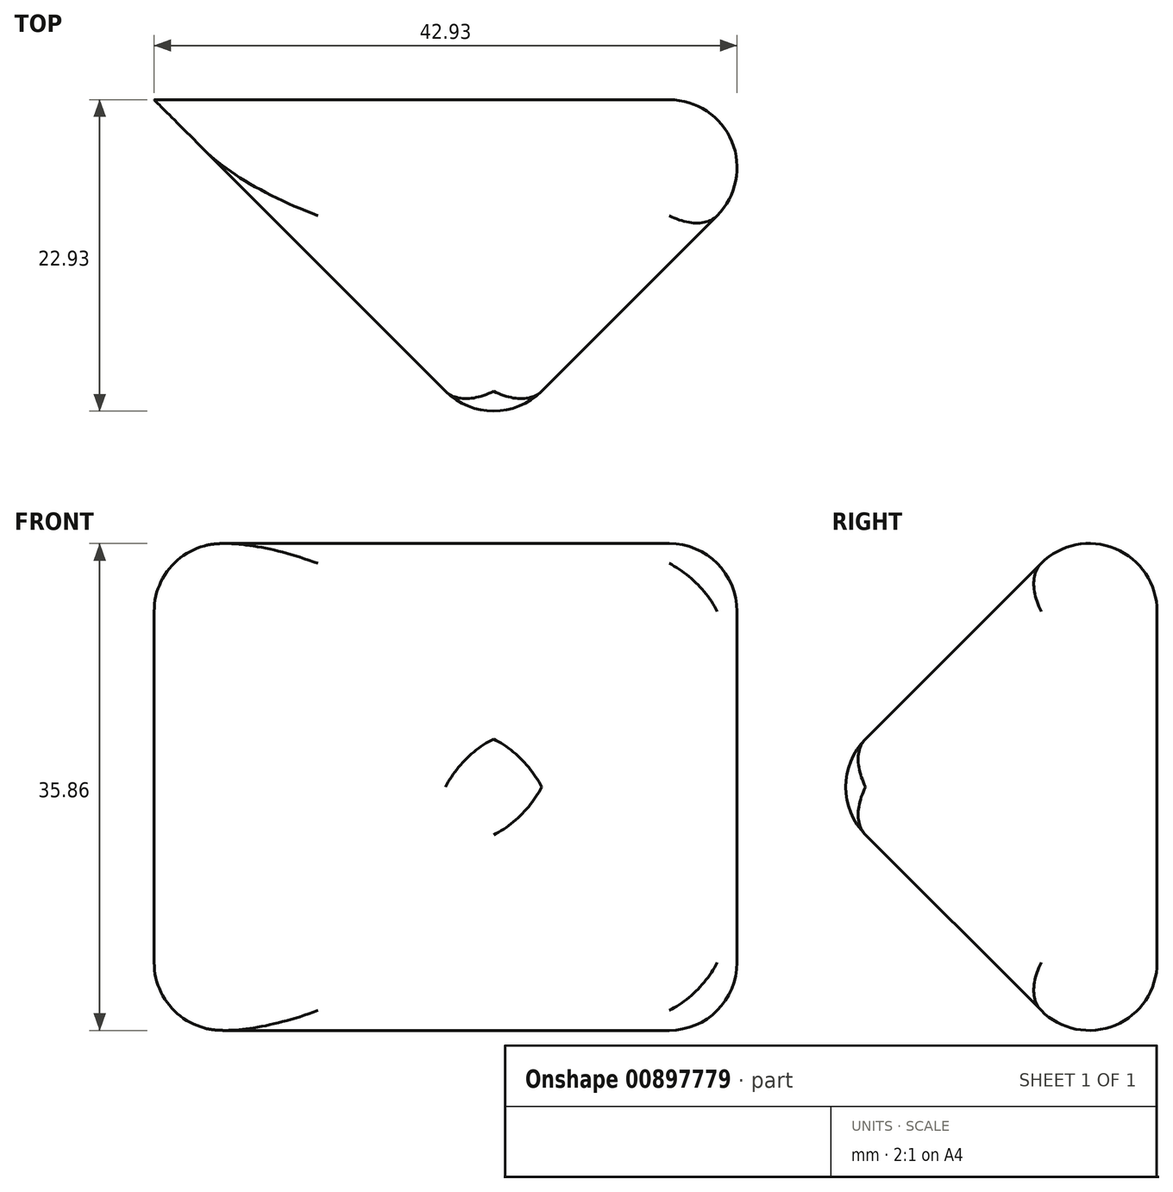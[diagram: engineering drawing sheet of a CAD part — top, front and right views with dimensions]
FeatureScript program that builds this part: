
annotation { "Feature Type Name" : "Feature", "Feature Type Description" : "" }
export const myFeature = defineFeature(function(context is Context, id is Id, definition is map)
    precondition{}
    {
        {
            var Q0;
            Q0=qCreatedBy(makeId("Front.planeOp"),FACE);
            var sketch = newSketch(context, id + "F0", { "sketchPlane" : qUnion([Q0])});
            skLineSegment(sketch, "E0.bottom", {"start": v(-50, 50) * mm, "end": v(0, 50) * mm});
            skLineSegment(sketch, "E0.top", {"start": v(-50, 0) * mm, "end": v(0, 0) * mm});
            skLineSegment(sketch, "E0.left", {"start": v(-50, 50) * mm, "end": v(-50, 0) * mm});
            skLineSegment(sketch, "E0.right", {"start": v(0, 50) * mm, "end": v(0, 0) * mm});
            skSolve(sketch);
        }
        {
            var Q0;
            Q0 = qSketchRegion(id + "F0", true);
            extrude(context, id + "F1", {"entities" : qUnion([Q0]), "depth" : 25 * mm, "offsetDistance" : 25 * mm, "hasDraft" : true, "draftAngle" : 45 * degree, "draftPullDirection" : true});
        }
        {
            var Q0;
            Q0=makeQuery(id+"F1.opExtrude","SWEPT_FACE",FACE,{"disambiguationData":[OSD([sQuery(id+"F0.wireOp",EDGE,"E0.top")])]});
            var Q1;
            Q1=makeQuery(id+"F1.opExtrude","SWEPT_FACE",FACE,{"disambiguationData":[OSD([sQuery(id+"F0.wireOp",EDGE,"E0.right")])]});
            var Q2;
            Q2=makeQuery(id+"F1.opExtrude","SWEPT_FACE",FACE,{"disambiguationData":[OSD([sQuery(id+"F0.wireOp",EDGE,"E0.bottom")])]});
            var Q3;
            Q3=makeQuery(id+"F1.opExtrude","SWEPT_EDGE",EDGE,{"disambiguationData":[OSD([sQuery(id+"F0.wireOp",EDGE,"E0.bottom"),sQuery(id+"F0.wireOp",EDGE,"E0.left")])]});
            var Q4;
            {var subQ0=sQuery(id+"F0.wireOp",EDGE,"E0.left");Q4=makeQuery(id+"F1.*.draft.opDraft","MERGE",FACE,{"derivedFrom":[makeQuery(id+"F1.opExtrude","CAP_FACE",FACE,{"disambiguationData":[OSD([sQuery(id+"F0.wireOp",EDGE,"E0.bottom"),sQuery(id+"F0.wireOp",EDGE,"E0.top"),subQ0,sQuery(id+"F0.wireOp",EDGE,"E0.right")])],"isStart":false}),makeQuery(id+"F1.opExtrude","SWEPT_FACE",FACE,{"disambiguationData":[OSD([subQ0])]})]});}
            fillet(context, id + "F2", {"entities" : qUnion([Q0, Q1, Q2, Q3, Q4]), "radius" : 5 * mm, "tangentPropagation" : true, "allowEdgeOverflow" : false});
        }
    });
